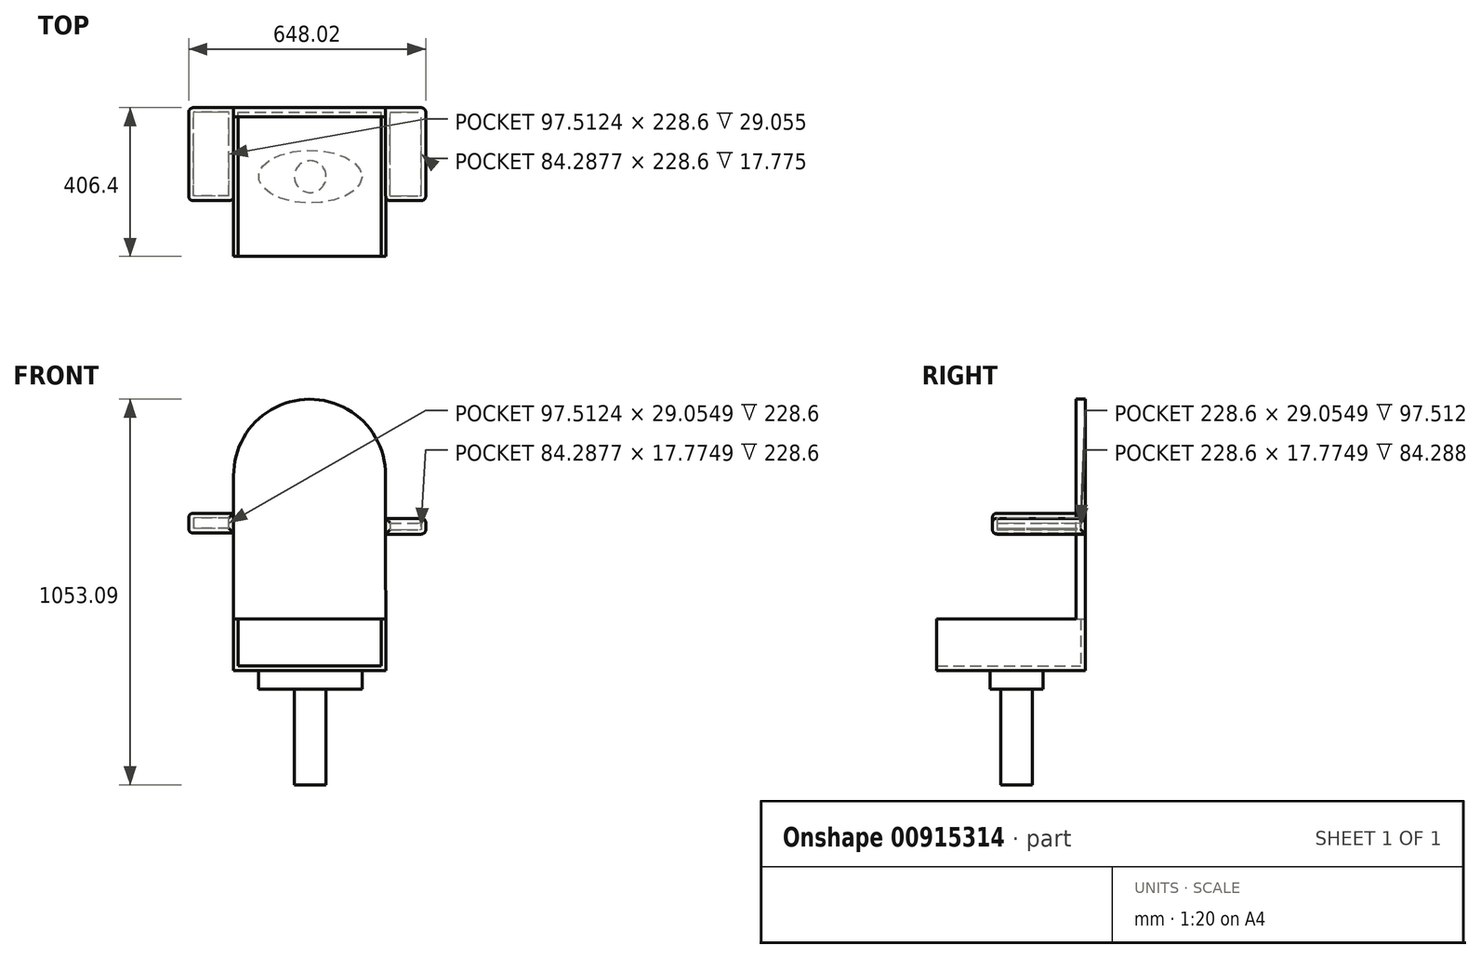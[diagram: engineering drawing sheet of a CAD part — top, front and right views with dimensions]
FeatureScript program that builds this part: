
annotation { "Feature Type Name" : "Feature", "Feature Type Description" : "" }
export const myFeature = defineFeature(function(context is Context, id is Id, definition is map)
    precondition{}
    {
        {
            var Q0;
            Q0=qCreatedBy(makeId("Front.planeOp"),FACE);
            var Q1;
            Q1=qCreatedBy(makeId("Front.planeOp"),FACE);
            var sketch = newSketch(context, id + "F0", { "sketchPlane" : qUnion([Q0, Q1])});
            skLineSegment(sketch, "E0", {"start": v(-327.3, 156.22) * mm, "end": v(-327.3, 391.15) * mm});
            skLineSegment(sketch, "E1", {"start": v(88.12, 392.7) * mm, "end": v(88.12, 157.77) * mm});
            skArc(sketch, "E2", {"start": v(88.12, 392.7) * mm, "mid": v(-120.37, 600.42) * mm, "end": v(-327.3, 391.15) * mm});
            skLineSegment(sketch, "E3", {"start": v(-327.3, 156.22) * mm, "end": v(-327.3, 0) * mm});
            skLineSegment(sketch, "E4", {"start": v(-327.3, 0) * mm, "end": v(88.9, 0) * mm});
            skLineSegment(sketch, "E5", {"start": v(88.9, 0) * mm, "end": v(88.12, 157.77) * mm});
            skSolve(sketch);
        }
        {
            var Q0;
            Q0=makeQuery(id+"F0.imprint","IMPRINT",FACE,{"disambiguationData":[TD([[makeQuery(id+"F0.imprint","IMPRINT",EDGE,{"derivedFrom":sQuery(id+"F0.wireOp",EDGE,"E0")}),-1.0]])]});
            extrude(context, id + "F1", {"entities" : qUnion([Q0]), "depth" : 25.4 * mm, "offsetDistance" : 25.4 * mm});
        }
        {
            var Q0;
            Q0=qCreatedBy(makeId("Front.planeOp"),FACE);
            var sketch = newSketch(context, id + "F2", { "sketchPlane" : qUnion([Q0])});
            skLineSegment(sketch, "E6.bottom", {"start": v(88.12, 275.24) * mm, "end": v(197.8, 275.24) * mm});
            skLineSegment(sketch, "E6.top", {"start": v(88.12, 232.07) * mm, "end": v(197.8, 232.07) * mm});
            skLineSegment(sketch, "E6.left", {"start": v(88.12, 275.24) * mm, "end": v(88.12, 232.07) * mm});
            skLineSegment(sketch, "E6.right", {"start": v(197.8, 275.24) * mm, "end": v(197.8, 232.07) * mm});
            skLineSegment(sketch, "E7.bottom", {"start": v(-327.3, 289.24) * mm, "end": v(-450.2, 289.24) * mm});
            skLineSegment(sketch, "E7.top", {"start": v(-327.3, 234.79) * mm, "end": v(-450.2, 234.79) * mm});
            skLineSegment(sketch, "E7.left", {"start": v(-327.3, 289.24) * mm, "end": v(-327.3, 234.79) * mm});
            skLineSegment(sketch, "E7.right", {"start": v(-450.2, 289.24) * mm, "end": v(-450.2, 234.79) * mm});
            skSolve(sketch);
        }
        {
            var Q0;
            Q0=makeQuery(id+"F2.imprint","IMPRINT",FACE,{"disambiguationData":[TD([[makeQuery(id+"F2.imprint","IMPRINT",EDGE,{"derivedFrom":sQuery(id+"F2.wireOp",EDGE,"E7.bottom")}),1.0]])]});
            var Q1;
            Q1=makeQuery(id+"F2.imprint","IMPRINT",FACE,{"disambiguationData":[TD([[makeQuery(id+"F2.imprint","IMPRINT",EDGE,{"derivedFrom":sQuery(id+"F2.wireOp",EDGE,"E6.bottom")}),-1.0]])]});
            extrude(context, id + "F3", {"entities" : qUnion([Q0, Q1]), "operationType" : NewBodyOperationType.ADD, "depth" : 25.4 * mm, "offsetDistance" : 25.4 * mm});
        }
        {
            var Q0;
            Q0 = qSketchRegion(id + "F2", true);
            extrude(context, id + "F4", {"entities" : qUnion([Q0]), "operationType" : NewBodyOperationType.ADD, "depth" : 254 * mm, "offsetDistance" : 25.4 * mm});
        }
        {
            var Q0;
            Q0=qCreatedBy(makeId("Front.planeOp"),FACE);
            var sketch = newSketch(context, id + "F5", { "sketchPlane" : qUnion([Q0])});
            skLineSegment(sketch, "E8.bottom", {"start": v(-327.68, 0) * mm, "end": v(88.9, 0) * mm});
            skLineSegment(sketch, "E8.top", {"start": v(-327.68, -140.25) * mm, "end": v(88.9, -140.25) * mm});
            skLineSegment(sketch, "E8.left", {"start": v(-327.68, 0) * mm, "end": v(-327.68, -140.25) * mm});
            skLineSegment(sketch, "E8.right", {"start": v(88.9, 0) * mm, "end": v(88.9, -140.25) * mm});
            skSolve(sketch);
        }
        {
            var Q0;
            Q0=makeQuery(id+"F5.imprint","IMPRINT",FACE,{"disambiguationData":[TD([[makeQuery(id+"F5.imprint","IMPRINT",EDGE,{"derivedFrom":sQuery(id+"F5.wireOp",EDGE,"E8.bottom")}),-1.0]])]});
            extrude(context, id + "F6", {"entities" : qUnion([Q0]), "operationType" : NewBodyOperationType.ADD, "depth" : 406.4 * mm, "offsetDistance" : 25.4 * mm});
        }
        {
            var Q0;
            Q0=makeQuery(id+"F6.opExtrude","CAP_FACE",FACE,{"disambiguationData":[OSD([sQuery(id+"F5.wireOp",EDGE,"E8.bottom"),sQuery(id+"F5.wireOp",EDGE,"E8.top"),sQuery(id+"F5.wireOp",EDGE,"E8.left"),sQuery(id+"F5.wireOp",EDGE,"E8.right")])],"isStart":false});
            var Q1;
            Q1=makeQuery(id+"F6.opExtrude","SWEPT_FACE",FACE,{"disambiguationData":[OSD([sQuery(id+"F5.wireOp",EDGE,"E8.bottom")])]});
            shell(context, id + "F7", {"entities" : qUnion([Q0, Q1]), "thickness" : 12.7 * mm});
        }
        {
            var Q0;
            Q0=makeQuery(id+"F6.opExtrude","SWEPT_FACE",FACE,{"disambiguationData":[OSD([sQuery(id+"F5.wireOp",EDGE,"E8.top")])]});
            var sketch = newSketch(context, id + "F8", { "sketchPlane" : qUnion([Q0])});
            skEllipse(sketch, "E9", {"center": v(-118.03, 188.28) * mm, "majorRadius": 141.58 * mm, "minorRadius": 72.14 * mm, "majorAxis": v(1, 0)});
            skSolve(sketch);
        }
        {
            var Q0;
            Q0=makeQuery(id+"F8.imprint","IMPRINT",FACE,{"disambiguationData":[TD([[makeQuery(id+"F8.imprint","IMPRINT",EDGE,{"derivedFrom":sQuery(id+"F8.wireOp",EDGE,"E9")}),1.0]])]});
            extrude(context, id + "F9", {"entities" : qUnion([Q0]), "operationType" : NewBodyOperationType.ADD, "depth" : 50.8 * mm, "offsetDistance" : 25.4 * mm});
        }
        {
            var Q0;
            Q0=makeQuery(id+"F9.opExtrude","CAP_FACE",FACE,{"disambiguationData":[OSD([sQuery(id+"F8.wireOp",EDGE,"E9")])],"isStart":false});
            var sketch = newSketch(context, id + "F10", { "sketchPlane" : qUnion([Q0])});
            skCircle(sketch, "E10", {"center": v(-118.03, 188.28) * mm, "radius": 43.45 * mm});
            skSolve(sketch);
        }
        {
            var Q0;
            Q0 = qSketchRegion(id + "F10", true);
            extrude(context, id + "F11", {"entities" : qUnion([Q0]), "operationType" : NewBodyOperationType.ADD, "depth" : 261.62 * mm, "offsetDistance" : 25.4 * mm});
        }
        {
            var Q0;
            Q0=makeQuery(id+"F4.opExtrude","CAP_FACE",FACE,{"disambiguationData":[OSD([sQuery(id+"F2.wireOp",EDGE,"E6.bottom"),sQuery(id+"F2.wireOp",EDGE,"E6.top"),sQuery(id+"F2.wireOp",EDGE,"E6.left"),sQuery(id+"F2.wireOp",EDGE,"E6.right")])],"isStart":false});
            fillet(context, id + "F12", {"entities" : qUnion([Q0]), "radius" : 12.7 * mm, "tangentPropagation" : true, "allowEdgeOverflow" : false});
        }
        {
            var Q0;
            Q0=makeQuery(id+"F4.opExtrude","CAP_FACE",FACE,{"disambiguationData":[OSD([sQuery(id+"F2.wireOp",EDGE,"E7.bottom"),sQuery(id+"F2.wireOp",EDGE,"E7.top"),sQuery(id+"F2.wireOp",EDGE,"E7.left"),sQuery(id+"F2.wireOp",EDGE,"E7.right")])],"isStart":false});
            fillet(context, id + "F13", {"entities" : qUnion([Q0]), "radius" : 12.7 * mm, "tangentPropagation" : true, "allowEdgeOverflow" : false});
        }
        {
            var Q0;
            {var subQ0=sQuery(id+"F2.wireOp",EDGE,"E6.right");Q0=makeQuery(id+"F4.boolean.opBoolean","MERGE",FACE,{"derivedFrom":[makeQuery(id+"F3.opExtrude","SWEPT_FACE",FACE,{"disambiguationData":[OSD([subQ0])]}),makeQuery(id+"F4.opExtrude","SWEPT_FACE",FACE,{"disambiguationData":[OSD([subQ0])]})]});}
            fillet(context, id + "F14", {"entities" : qUnion([Q0]), "radius" : 12.7 * mm, "tangentPropagation" : true, "allowEdgeOverflow" : false});
        }
        {
            var Q0;
            {var subQ0=sQuery(id+"F2.wireOp",EDGE,"E7.right");Q0=makeQuery(id+"F4.boolean.opBoolean","MERGE",FACE,{"derivedFrom":[makeQuery(id+"F3.opExtrude","SWEPT_FACE",FACE,{"disambiguationData":[OSD([subQ0])]}),makeQuery(id+"F4.opExtrude","SWEPT_FACE",FACE,{"disambiguationData":[OSD([subQ0])]})]});}
            fillet(context, id + "F15", {"entities" : qUnion([Q0]), "radius" : 12.7 * mm, "tangentPropagation" : true, "allowEdgeOverflow" : false});
        }
    });
